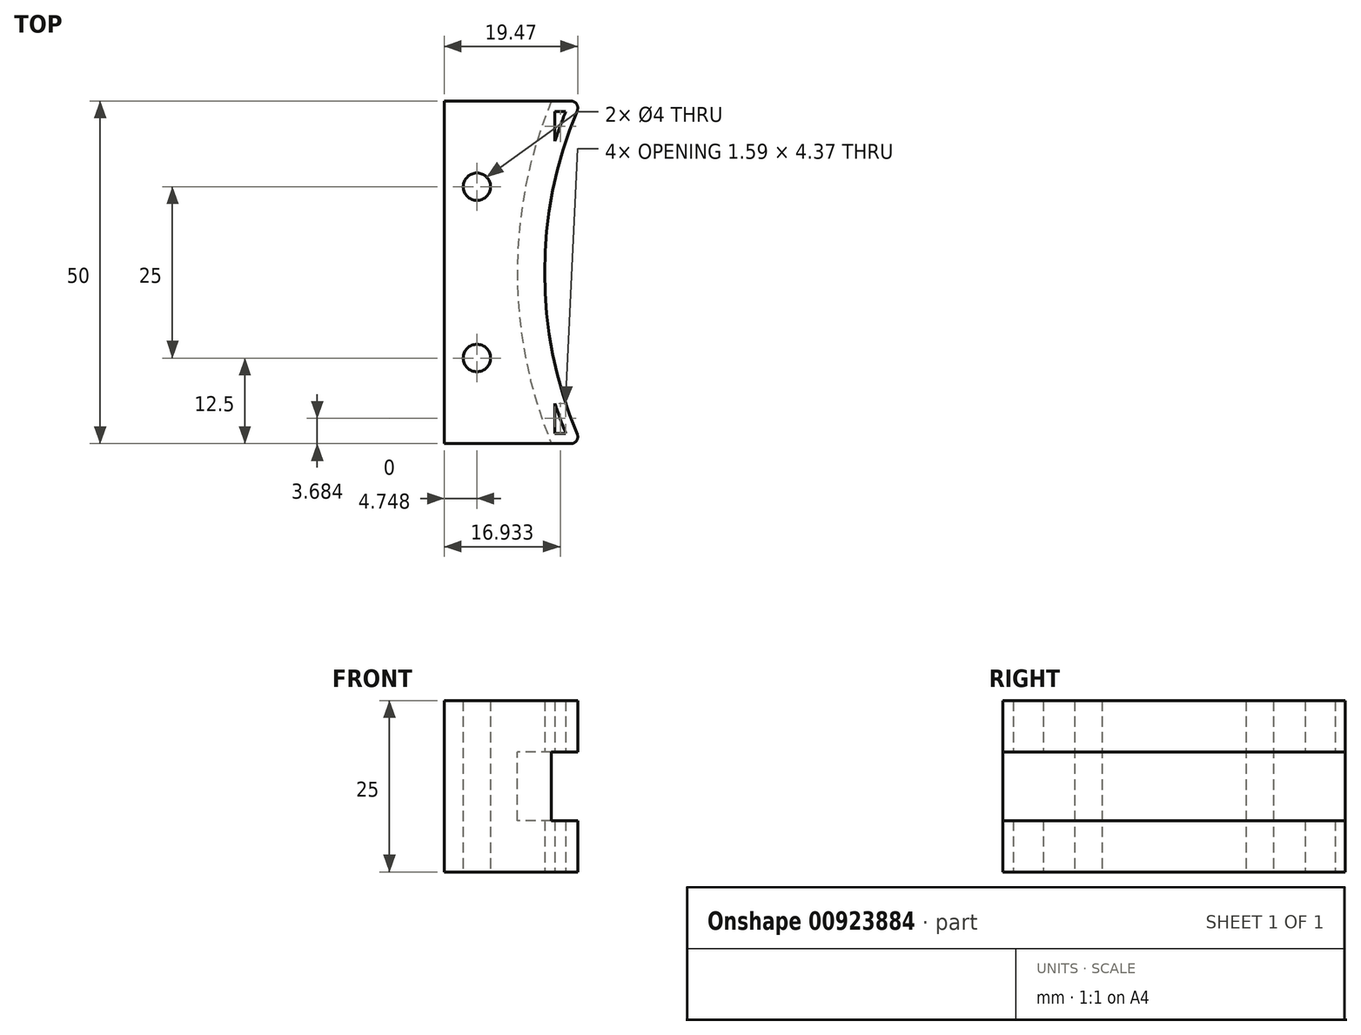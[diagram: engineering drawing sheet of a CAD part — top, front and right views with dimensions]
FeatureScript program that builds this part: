
annotation { "Feature Type Name" : "Feature", "Feature Type Description" : "" }
export const myFeature = defineFeature(function(context is Context, id is Id, definition is map)
    precondition{}
    {
        {
            var Q0;
            Q0=qCreatedBy(makeId("Top.planeOp"),FACE);
            var sketch = newSketch(context, id + "F0", { "sketchPlane" : qUnion([Q0])});
            skArc(sketch, "E0", {"start": v(-55.64, 25) * mm, "mid": v(-61, 0) * mm, "end": v(-55.64, -25) * mm});
            skLineSegment(sketch, "E1.bottom", {"start": v(-55.64, 25) * mm, "end": v(55.64, 25) * mm});
            skLineSegment(sketch, "E1.top", {"start": v(-55.64, -25) * mm, "end": v(55.64, -25) * mm});
            skLineSegment(sketch, "E1.left", {"start": v(-55.64, 25) * mm, "end": v(-55.64, -25) * mm});
            skLineSegment(sketch, "E1.right", {"start": v(55.64, 25) * mm, "end": v(55.64, -25) * mm});
            skLineSegment(sketch, "E2.bottom", {"start": v(-55.64, -25) * mm, "end": v(-75.64, -25) * mm});
            skLineSegment(sketch, "E2.top", {"start": v(-55.64, 25) * mm, "end": v(-75.64, 25) * mm});
            skLineSegment(sketch, "E2.left", {"start": v(-55.64, -25) * mm, "end": v(-55.64, 25) * mm});
            skLineSegment(sketch, "E2.right", {"start": v(-75.64, -25) * mm, "end": v(-75.64, 25) * mm});
            skLineSegment(sketch, "E3", {"start": v(-61, 25) * mm, "end": v(-61, -25) * mm});
            skArc(sketch, "E4.trimOffspring", {"start": v(55.64, -25) * mm, "mid": v(61, 0) * mm, "end": v(55.64, 25) * mm});
            skLineSegment(sketch, "E5", {"start": v(-61, 25) * mm, "end": v(-61, 23.5) * mm, "construction": true});
            skLineSegment(sketch, "E6", {"start": v(-61, 25) * mm, "end": v(-59.5, 25) * mm, "construction": true});
            skLineSegment(sketch, "E7", {"start": v(-59.5, 23.5) * mm, "end": v(-59.5, 19.13) * mm});
            skLineSegment(sketch, "E8", {"start": v(-59.5, 23.5) * mm, "end": v(-57.91, 23.5) * mm});
            skArc(sketch, "E9.trimOffspring", {"start": v(-57.91, 23.5) * mm, "mid": v(-58.75, 21.33) * mm, "end": v(-59.5, 19.13) * mm});
            skLineSegment(sketch, "E10.bottom", {"start": v(-75.64, 25) * mm, "end": v(-70.9, 25) * mm, "construction": true});
            skLineSegment(sketch, "E10.top", {"start": v(-75.64, 17.5) * mm, "end": v(-70.9, 17.5) * mm, "construction": true});
            skLineSegment(sketch, "E10.left", {"start": v(-75.64, 25) * mm, "end": v(-75.64, 17.5) * mm, "construction": true});
            skLineSegment(sketch, "E10.right", {"start": v(-70.9, 25) * mm, "end": v(-70.9, 17.5) * mm, "construction": true});
            skLineSegment(sketch, "E11.bottom", {"start": v(-75.64, 0) * mm, "end": v(-70.9, 0) * mm, "construction": true});
            skLineSegment(sketch, "E11.top", {"start": v(-75.64, 7.5) * mm, "end": v(-70.9, 7.5) * mm, "construction": true});
            skLineSegment(sketch, "E11.left", {"start": v(-75.64, 0) * mm, "end": v(-75.64, 7.5) * mm, "construction": true});
            skLineSegment(sketch, "E11.right", {"start": v(-70.9, 0) * mm, "end": v(-70.9, 7.5) * mm, "construction": true});
            skLineSegment(sketch, "E12", {"start": v(-75.64, 0) * mm, "end": v(-61, 0) * mm});
            skLineSegment(sketch, "E13.MirrorCS", {"start": v(-59.5, -23.5) * mm, "end": v(-59.5, -19.13) * mm});
            skLineSegment(sketch, "E14.MirrorCS", {"start": v(-59.5, -23.5) * mm, "end": v(-57.91, -23.5) * mm});
            skArc(sketch, "E15.MirrorCS", {"start": v(-57.91, -23.5) * mm, "mid": v(-58.75, -21.33) * mm, "end": v(-59.5, -19.13) * mm});
            skLineSegment(sketch, "E16", {"start": v(-70.9, 17.5) * mm, "end": v(-70.9, 7.5) * mm, "construction": true});
            skCircle(sketch, "E17", {"center": v(-70.9, 12.5) * mm, "radius": 2 * mm});
            skCircle(sketch, "E18.MirrorC", {"center": v(-70.9, -12.5) * mm, "radius": 2 * mm});
            skSolve(sketch);
        }
        {
            var Q0;
            Q0=qCreatedBy(makeId("Front.planeOp"),FACE);
            var sketch = newSketch(context, id + "F1", { "sketchPlane" : qUnion([Q0])});
            skLineSegment(sketch, "E19", {"start": v(-61, 0) * mm, "end": v(-61, 12.5) * mm, "construction": true});
            skLineSegment(sketch, "E20.bottom", {"start": v(-65, 7.5) * mm, "end": v(-57, 7.5) * mm});
            skLineSegment(sketch, "E20.top", {"start": v(-65, 17.5) * mm, "end": v(-57, 17.5) * mm});
            skLineSegment(sketch, "E20.left", {"start": v(-65, 7.5) * mm, "end": v(-65, 17.5) * mm});
            skLineSegment(sketch, "E20.right", {"start": v(-57, 7.5) * mm, "end": v(-57, 17.5) * mm});
            skPoint(sketch, "E20.middle", {"position": v(-61, 12.5) * mm});
            skLineSegment(sketch, "E21", {"start": v(0, 0) * mm, "end": v(0, 30.4) * mm, "construction": true});
            skSolve(sketch);
        }
        {
            var Q0;
            Q0=makeQuery(id+"F0.imprint","IMPRINT",FACE,{"disambiguationData":[TD([[makeQuery(id+"F0.imprint","IMPRINT",EDGE,{"derivedFrom":sQuery(id+"F0.wireOp",EDGE,"E7")}),-1.0]])]});
            var Q1;
            Q1=makeQuery(id+"F0.imprint","IMPRINT",FACE,{"disambiguationData":[TD([[makeQuery(id+"F0.imprint","IMPRINT",EDGE,{"derivedFrom":sQuery(id+"F0.wireOp",EDGE,"E13.MirrorCS")}),1.0]])]});
            var Q2;
            {var subQ3=sQuery(id+"F0.wireOp",EDGE,"E12");Q2=makeQuery(id+"F0.imprint","IMPRINT",FACE,{"disambiguationData":[TD([[makeQuery(id+"F0.imprint","IMPRINT",EDGE,{"derivedFrom":subQ3}),-1.0]])]});}
            var Q3;
            Q3=makeQuery(id+"F0.imprint","IMPRINT",FACE,{"disambiguationData":[TD([[makeQuery(id+"F0.imprint","IMPRINT",EDGE,{"derivedFrom":sQuery(id+"F0.wireOp",EDGE,"PVW8i8Wt-0xkI-O4RV-OvAW-XAR8i21FIH9G")}),-1.0]])]});
            var Q4;
            {var subQ3=sQuery(id+"F0.wireOp",EDGE,"E12");Q4=makeQuery(id+"F0.imprint","IMPRINT",FACE,{"disambiguationData":[TD([[makeQuery(id+"F0.imprint","IMPRINT",EDGE,{"derivedFrom":subQ3}),1.0]])]});}
            extrude(context, id + "F2", {"entities" : qUnion([Q0, Q1, Q2, Q3, Q4]), "depth" : 25 * mm, "offsetDistance" : 25 * mm});
        }
        {
            var Q0;
            Q0=makeQuery(id+"F1.imprint","IMPRINT",FACE,{"disambiguationData":[TD([[makeQuery(id+"F1.imprint","IMPRINT",EDGE,{"derivedFrom":sQuery(id+"F1.wireOp",EDGE,"E20.bottom")}),1.0]])]});
            var Q1;
            Q1=sQuery(id+"F1.wireOp",EDGE,"E21");
            revolve(context, id + "F3", {"operationType" : NewBodyOperationType.REMOVE, "surfaceOperationType" : NewSurfaceOperationType.NEW, "entities" : qUnion([Q0]), "axis" : qUnion([Q1]), "revolveType" : RevolveType.FULL, "oppositeDirection" : true});
        }
        {
            var Q0;
            {var subQ0=sQuery(id+"F0.wireOp",EDGE,"E0");var subQ1=sQuery(id+"F0.wireOp",EDGE,"E2.top");Q0=makeQuery(id+"F3.boolean.opBoolean","SPLIT",EDGE,{"disambiguationData":[TD([makeQuery(id+"F3.opRevolve","SWEPT_FACE",FACE,{"disambiguationData":[OSD([sQuery(id+"F1.wireOp",EDGE,"E20.top")])]})])],"derivedFrom":makeQuery(id+"F2.opExtrude","SWEPT_EDGE",EDGE,{"disambiguationData":[OSD([subQ0,sQuery(id+"F0.wireOp",EDGE,"E1.bottom"),subQ1,sQuery(id+"F0.wireOp",EDGE,"E2.left")])]})});}
            var Q1;
            {var subQ0=sQuery(id+"F0.wireOp",EDGE,"E0");var subQ1=sQuery(id+"F0.wireOp",EDGE,"E2.top");Q1=makeQuery(id+"F3.boolean.opBoolean","SPLIT",EDGE,{"disambiguationData":[TD([makeQuery(id+"F3.opRevolve","SWEPT_FACE",FACE,{"disambiguationData":[OSD([sQuery(id+"F1.wireOp",EDGE,"E20.bottom")])]})])],"derivedFrom":makeQuery(id+"F2.opExtrude","SWEPT_EDGE",EDGE,{"disambiguationData":[OSD([subQ0,sQuery(id+"F0.wireOp",EDGE,"E1.bottom"),subQ1,sQuery(id+"F0.wireOp",EDGE,"E2.left")])]})});}
            var Q2;
            {var subQ0=sQuery(id+"F0.wireOp",EDGE,"E0");var subQ1=sQuery(id+"F0.wireOp",EDGE,"E2.bottom");Q2=makeQuery(id+"F3.boolean.opBoolean","SPLIT",EDGE,{"disambiguationData":[TD([makeQuery(id+"F3.opRevolve","SWEPT_FACE",FACE,{"disambiguationData":[OSD([sQuery(id+"F1.wireOp",EDGE,"E20.bottom")])]})])],"derivedFrom":makeQuery(id+"F2.opExtrude","SWEPT_EDGE",EDGE,{"disambiguationData":[OSD([subQ0,sQuery(id+"F0.wireOp",EDGE,"E1.top"),subQ1,sQuery(id+"F0.wireOp",EDGE,"E2.left")])]})});}
            var Q3;
            {var subQ0=sQuery(id+"F0.wireOp",EDGE,"E0");var subQ1=sQuery(id+"F0.wireOp",EDGE,"E2.bottom");Q3=makeQuery(id+"F3.boolean.opBoolean","SPLIT",EDGE,{"disambiguationData":[TD([makeQuery(id+"F3.opRevolve","SWEPT_FACE",FACE,{"disambiguationData":[OSD([sQuery(id+"F1.wireOp",EDGE,"E20.top")])]})])],"derivedFrom":makeQuery(id+"F2.opExtrude","SWEPT_EDGE",EDGE,{"disambiguationData":[OSD([subQ0,sQuery(id+"F0.wireOp",EDGE,"E1.top"),subQ1,sQuery(id+"F0.wireOp",EDGE,"E2.left")])]})});}
            fillet(context, id + "F4", {"entities" : qUnion([Q0, Q1, Q2, Q3]), "radius" : 1 * mm, "tangentPropagation" : true, "allowEdgeOverflow" : false});
        }
    });
